# Revit family: GRAS_HWG-33NW-KP-20-30 HS (W)
name_source: partatom
category: Osprzęt hydrauliczny
revit_build: Autodesk Revit 2018 (Build: 20190510_1515(x64)
units: mm (PartAtom-declared; Revit-internal decimal feet)

## family parameters
Obiekt nadrzędny = Powierzchnia
Punkt obliczania pomieszczeń = Nie
Tnij formami wycięć po wczytaniu = Nie
Typ części = Normalny
Współdzielony = Nie
Wymiar okrągłego złącza = Użyj średnicy

## types (2) — shared parameters
Cabinet_Depth = 290 mm  [stored 0.951444 ft]
Cabinet_Height = 1025 mm  [stored 3.36286 ft]
Cabinet_Material = DC01, RAL3000
Cabinet_Width = 795 mm  [stored 2.60827 ft]
D1 = 100 mm  [stored 0.328084 ft]
DN = 33 mm  [stored 0.108268 ft]
Flow = 114.0 L/s
H1 = 100 mm  [stored 0.328084 ft]
Hole_Depth = 300 mm
Hole_Height = 1045 mm
Hole_Width = 815 mm
K_factor = 42
Model = HWG-33NW-KP-20/30 HS (W), RAL3000
Opis = http://gras.pl
Producent = GRAS PPPH
URL = http://www.gras.pl
W1 = 100 mm  [stored 0.328084 ft]
picH = 60 mm  [stored 0.19685 ft]
zero-valued in all types: Domyślna rzędna, mounting_plane, zer0

## type names (no varying parameters)
- HWG-33NW-KP-20/30 HS (W), RAL9010
- HWG-33NW-KP-20/30 HS (W), RAL3000

note: [stored X ft] marks values corroborated as IEEE doubles in the binary element streams (Revit-internal decimal feet)

## geometry (parser evidence)
native form markers: Blend x4
no freeform markers — native parametric forms only
